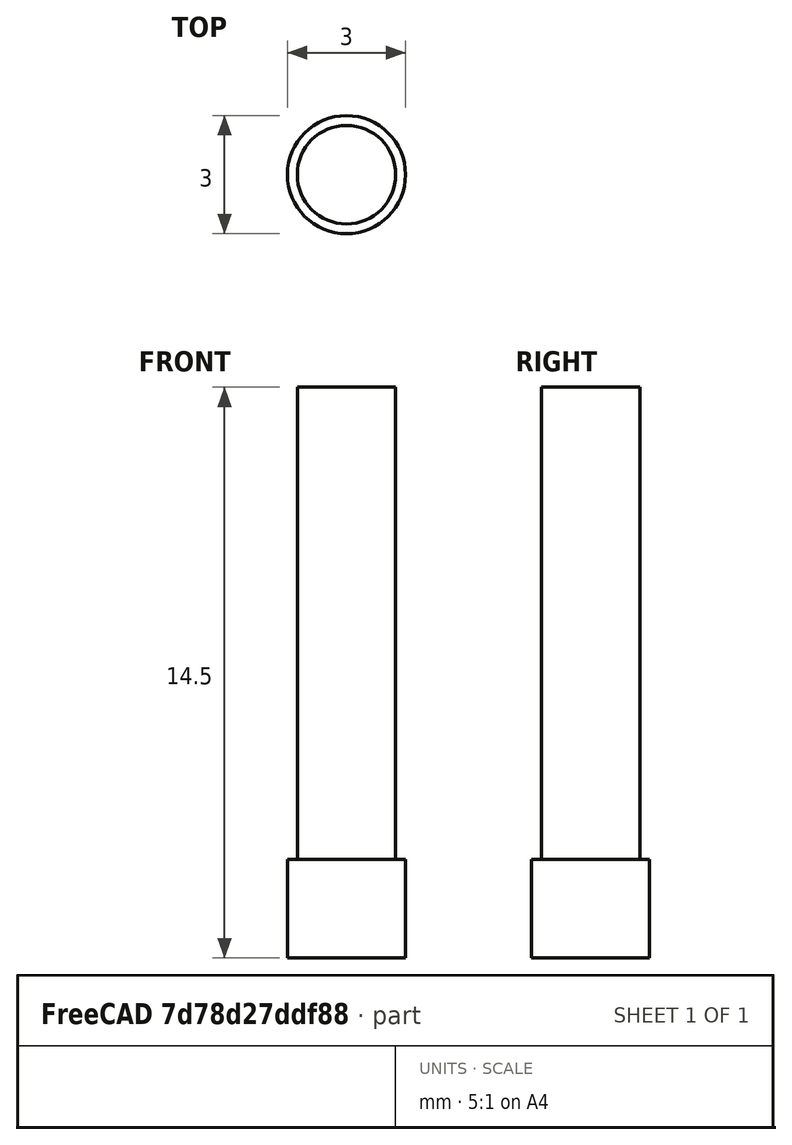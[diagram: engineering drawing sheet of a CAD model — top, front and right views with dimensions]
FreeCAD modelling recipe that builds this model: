
FCSTD DOCUMENT  (FreeCAD 0.18R)
Label: M2.5x12mm-worstCase
License: All rights reserved
LicenseURL: http://en.wikipedia.org/wiki/All_rights_reserved
objects: Sketcher::SketchObject×2, Part::Extrusion×2
note: 4 computed .brp shape members not serialized (recipe doc carries the construction recipe); baked Part::Feature solids carry a one-line shape summary decoded from their .brp

FEATURE [Sketcher::SketchObject] Sketch
  sketch-geometry (1):
    g0: Circle CenterX=0 CenterY=0 CenterZ=0 NormalX=0 NormalY=0 NormalZ=1 AngleXU=0 Radius=1.5
  constraints (2):
    c: Coincident(g0,g-1)
    c: Radius(g0) = 1.5
FEATURE [Part::Extrusion] Extrude
  Base = -> Sketch
  Dir = (0,0,1)
  DirMode = 2
  FaceMakerClass = Part::FaceMakerBullseye
  LengthFwd = -2.5
  LengthRev = 0
  Solid = true
  Symmetric = false
FEATURE [Sketcher::SketchObject] Sketch001
  sketch-geometry (1):
    g0: Circle CenterX=0 CenterY=0 CenterZ=0 NormalX=0 NormalY=0 NormalZ=1 AngleXU=0 Radius=1.25
  constraints (2):
    c: Coincident(g0,g-1)
    c: Radius(g0) = 1.25
FEATURE [Part::Extrusion] Extrude001
  Base = -> Sketch001
  Dir = (0,0,1)
  DirMode = 2
  FaceMakerClass = Part::FaceMakerBullseye
  LengthFwd = 12
  LengthRev = 0
  Solid = true
  Symmetric = false
